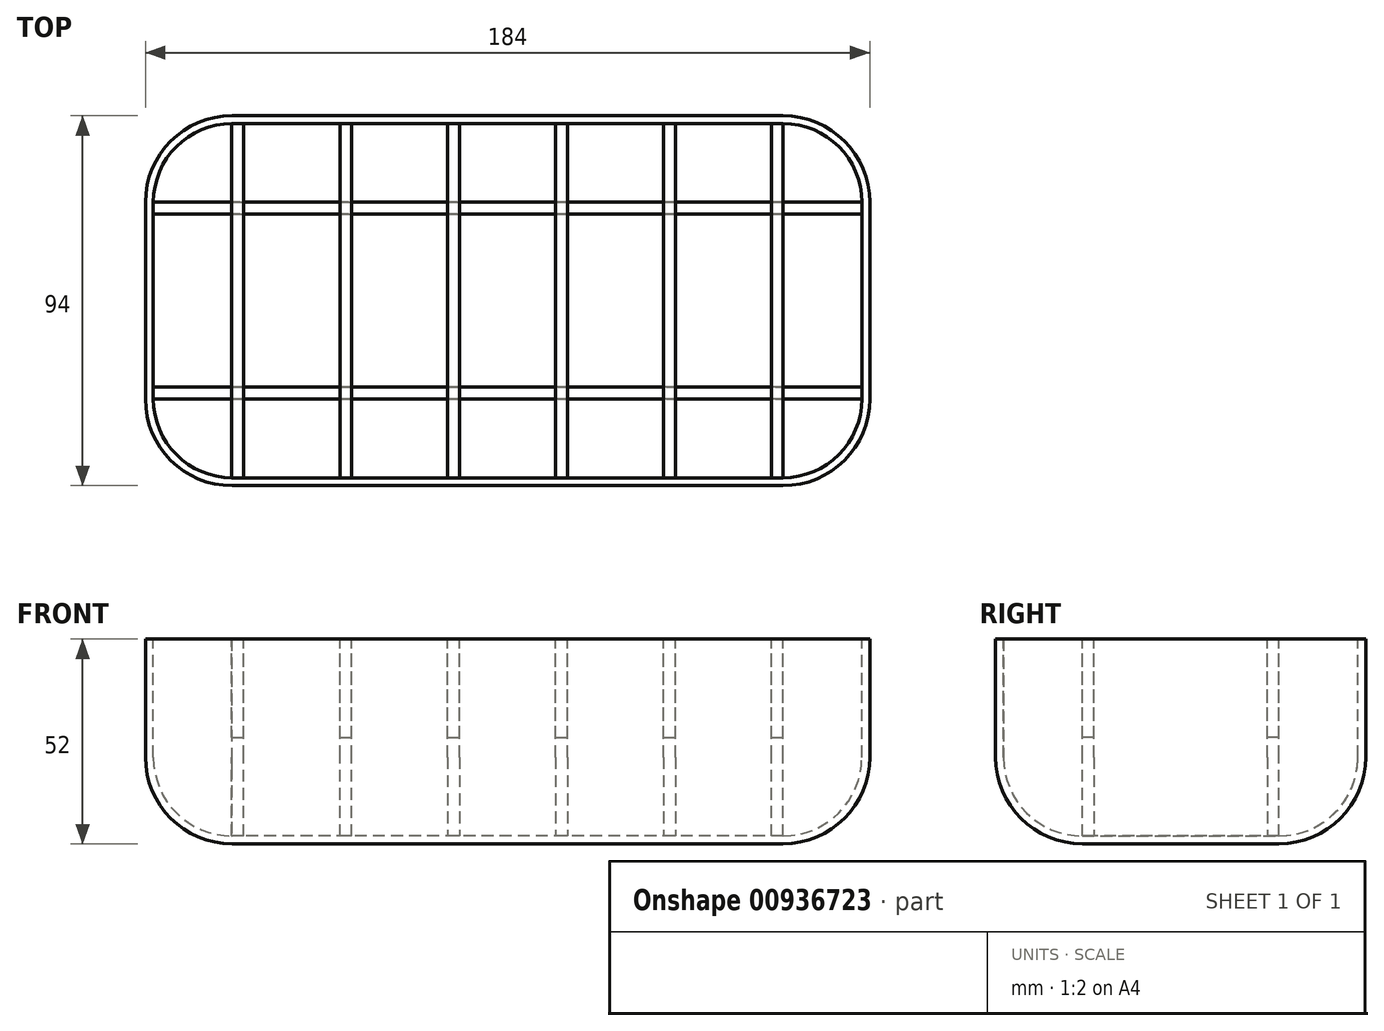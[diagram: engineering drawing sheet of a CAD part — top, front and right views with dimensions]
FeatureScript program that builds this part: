
annotation { "Feature Type Name" : "Feature", "Feature Type Description" : "" }
export const myFeature = defineFeature(function(context is Context, id is Id, definition is map)
    precondition{}
    {
        {
            var Q0;
            Q0=qCreatedBy(makeId("Top.planeOp"),FACE);
            var sketch = newSketch(context, id + "F0", { "sketchPlane" : qUnion([Q0])});
            skLineSegment(sketch, "E0.bottom", {"start": v(90, 45) * mm, "end": v(-90, 45) * mm});
            skLineSegment(sketch, "E0.top", {"start": v(90, -45) * mm, "end": v(-90, -45) * mm});
            skLineSegment(sketch, "E0.left", {"start": v(90, 45) * mm, "end": v(90, -45) * mm});
            skLineSegment(sketch, "E0.right", {"start": v(-90, 45) * mm, "end": v(-90, -45) * mm});
            skPoint(sketch, "E0.middle", {"position": v(0, 0) * mm});
            skSolve(sketch);
        }
        {
            var Q0;
            Q0=makeQuery(id+"F0.imprint","IMPRINT",FACE,{"disambiguationData":[TD([[makeQuery(id+"F0.imprint","IMPRINT",EDGE,{"derivedFrom":sQuery(id+"F0.wireOp",EDGE,"E0.bottom")}),1.0]])]});
            extrude(context, id + "F1", {"entities" : qUnion([Q0]), "oppositeDirection" : true, "depth" : 50 * mm, "offsetDistance" : 25 * mm});
        }
        {
            var Q0;
            Q0=makeQuery(id+"F1.opExtrude","CAP_EDGE",EDGE,{"disambiguationData":[OSD([sQuery(id+"F0.wireOp",EDGE,"E0.top")])],"isStart":false});
            var Q1;
            Q1=makeQuery(id+"F1.opExtrude","CAP_EDGE",EDGE,{"disambiguationData":[OSD([sQuery(id+"F0.wireOp",EDGE,"E0.left")])],"isStart":false});
            var Q2;
            Q2=makeQuery(id+"F1.opExtrude","CAP_EDGE",EDGE,{"disambiguationData":[OSD([sQuery(id+"F0.wireOp",EDGE,"E0.right")])],"isStart":false});
            var Q3;
            Q3=makeQuery(id+"F1.opExtrude","CAP_EDGE",EDGE,{"disambiguationData":[OSD([sQuery(id+"F0.wireOp",EDGE,"E0.bottom")])],"isStart":false});
            var Q4;
            Q4=makeQuery(id+"F1.opExtrude","SWEPT_EDGE",EDGE,{"disambiguationData":[OSD([sQuery(id+"F0.wireOp",EDGE,"E0.bottom"),sQuery(id+"F0.wireOp",EDGE,"E0.right")])]});
            var Q5;
            Q5=makeQuery(id+"F1.opExtrude","SWEPT_EDGE",EDGE,{"disambiguationData":[OSD([sQuery(id+"F0.wireOp",EDGE,"E0.bottom"),sQuery(id+"F0.wireOp",EDGE,"E0.left")])]});
            var Q6;
            Q6=makeQuery(id+"F1.opExtrude","SWEPT_EDGE",EDGE,{"disambiguationData":[OSD([sQuery(id+"F0.wireOp",EDGE,"E0.top"),sQuery(id+"F0.wireOp",EDGE,"E0.right")])]});
            var Q7;
            Q7=makeQuery(id+"F1.opExtrude","SWEPT_EDGE",EDGE,{"disambiguationData":[OSD([sQuery(id+"F0.wireOp",EDGE,"E0.top"),sQuery(id+"F0.wireOp",EDGE,"E0.left")])]});
            fillet(context, id + "F2", {"entities" : qUnion([Q0, Q1, Q2, Q3, Q4, Q5, Q6, Q7]), "radius" : 20 * mm, "tangentPropagation" : true, "allowEdgeOverflow" : false});
        }
        {
            var Q0;
            Q0=makeQuery(id+"F1.opExtrude","CAP_FACE",FACE,{"disambiguationData":[OSD([sQuery(id+"F0.wireOp",EDGE,"E0.bottom"),sQuery(id+"F0.wireOp",EDGE,"E0.top"),sQuery(id+"F0.wireOp",EDGE,"E0.left"),sQuery(id+"F0.wireOp",EDGE,"E0.right")])],"isStart":true});
            shell(context, id + "F3", {"entities" : qUnion([Q0]), "thickness" : 2 * mm, "oppositeDirection" : true});
        }
        {
            var Q0;
            Q0=makeQuery(id+"F1.opExtrude","CAP_FACE",FACE,{"disambiguationData":[OSD([sQuery(id+"F0.wireOp",EDGE,"E0.bottom"),sQuery(id+"F0.wireOp",EDGE,"E0.top"),sQuery(id+"F0.wireOp",EDGE,"E0.left"),sQuery(id+"F0.wireOp",EDGE,"E0.right")])],"isStart":true});
            var sketch = newSketch(context, id + "F4", { "sketchPlane" : qUnion([Q0])});
            skLineSegment(sketch, "E1", {"start": v(-90, 25) * mm, "end": v(90, 25) * mm});
            skLineSegment(sketch, "E2", {"start": v(90, -25) * mm, "end": v(-90, -25) * mm});
            skLineSegment(sketch, "E3", {"start": v(70, 45) * mm, "end": v(70, -45) * mm});
            skLineSegment(sketch, "E4.0", {"start": v(-67.06, 45) * mm, "end": v(-67.06, -45) * mm});
            skLineSegment(sketch, "E5.0", {"start": v(67, 45) * mm, "end": v(67, -45) * mm});
            skLineSegment(sketch, "E6.0", {"start": v(-90, 22) * mm, "end": v(90, 22) * mm});
            skLineSegment(sketch, "E7.0", {"start": v(90, -22) * mm, "end": v(-90, -22) * mm});
            skLineSegment(sketch, "E8.0", {"start": v(42.6, 45) * mm, "end": v(42.6, -45) * mm});
            skLineSegment(sketch, "E9.0", {"start": v(39.6, 45) * mm, "end": v(39.6, -45) * mm});
            skLineSegment(sketch, "E10.0", {"start": v(15.2, 45) * mm, "end": v(15.2, -45) * mm});
            skLineSegment(sketch, "E11.0", {"start": v(12.2, 45) * mm, "end": v(12.2, -45) * mm});
            skLineSegment(sketch, "E12.0", {"start": v(-12.2, 45) * mm, "end": v(-12.2, -45) * mm});
            skLineSegment(sketch, "E13.0", {"start": v(-15.2, 45) * mm, "end": v(-15.2, -45) * mm});
            skLineSegment(sketch, "E14.0", {"start": v(-39.6, 45) * mm, "end": v(-39.6, -45) * mm});
            skLineSegment(sketch, "E15.0", {"start": v(-42.6, 45) * mm, "end": v(-42.6, -45) * mm});
            skLineSegment(sketch, "E16.0", {"start": v(-70.06, 45) * mm, "end": v(-70.06, -45) * mm});
            skSolve(sketch);
        }
        {
            var Q0;
            {var subQ0=sQuery(id+"F4.wireOp",EDGE,"E1");var subQ7=sQuery(id+"F4.wireOp",EDGE,"E3");var subQ8=makeQuery(id+"F4.imprint","INTERSECT",VERTEX,{"derivedFrom":[subQ0,subQ7]});Q0=makeQuery(id+"F4.imprint","IMPRINT",FACE,{"disambiguationData":[TD([[makeQuery(id+"F4.imprint","IMPRINT",EDGE,{"disambiguationData":[TD([[subQ8,-1.0]])],"derivedFrom":subQ7}),1.0]])]});}
            var Q1;
            {var subQ0=sQuery(id+"F4.wireOp",EDGE,"E8.0");var subQ1=sQuery(id+"F4.wireOp",EDGE,"E1");var subQ2=makeQuery(id+"F4.imprint","INTERSECT",VERTEX,{"derivedFrom":[subQ1,subQ0]});Q1=makeQuery(id+"F4.imprint","IMPRINT",FACE,{"disambiguationData":[TD([[makeQuery(id+"F4.imprint","IMPRINT",EDGE,{"disambiguationData":[TD([[subQ2,-1.0]])],"derivedFrom":subQ1}),-1.0]])]});}
            var Q2;
            {var subQ0=sQuery(id+"F4.wireOp",EDGE,"E5.0");var subQ1=sQuery(id+"F4.wireOp",EDGE,"E1");var subQ2=makeQuery(id+"F4.imprint","INTERSECT",VERTEX,{"derivedFrom":[subQ1,subQ0]});Q2=makeQuery(id+"F4.imprint","IMPRINT",FACE,{"disambiguationData":[TD([[makeQuery(id+"F4.imprint","IMPRINT",EDGE,{"disambiguationData":[TD([[subQ2,-1.0]])],"derivedFrom":subQ1}),-1.0]])]});}
            var Q3;
            {var subQ0=sQuery(id+"F4.wireOp",EDGE,"E9.0");var subQ1=sQuery(id+"F4.wireOp",EDGE,"E1");var subQ2=makeQuery(id+"F4.imprint","INTERSECT",VERTEX,{"derivedFrom":[subQ1,subQ0]});Q3=makeQuery(id+"F4.imprint","IMPRINT",FACE,{"disambiguationData":[TD([[makeQuery(id+"F4.imprint","IMPRINT",EDGE,{"disambiguationData":[TD([[subQ2,-1.0]])],"derivedFrom":subQ1}),-1.0]])]});}
            var Q4;
            {var subQ0=sQuery(id+"F4.wireOp",EDGE,"E11.0");var subQ1=sQuery(id+"F4.wireOp",EDGE,"E1");var subQ2=makeQuery(id+"F4.imprint","INTERSECT",VERTEX,{"derivedFrom":[subQ1,subQ0]});Q4=makeQuery(id+"F4.imprint","IMPRINT",FACE,{"disambiguationData":[TD([[makeQuery(id+"F4.imprint","IMPRINT",EDGE,{"disambiguationData":[TD([[subQ2,-1.0]])],"derivedFrom":subQ1}),-1.0]])]});}
            var Q5;
            {var subQ0=sQuery(id+"F4.wireOp",EDGE,"E10.0");var subQ1=sQuery(id+"F4.wireOp",EDGE,"E1");var subQ2=makeQuery(id+"F4.imprint","INTERSECT",VERTEX,{"derivedFrom":[subQ1,subQ0]});Q5=makeQuery(id+"F4.imprint","IMPRINT",FACE,{"disambiguationData":[TD([[makeQuery(id+"F4.imprint","IMPRINT",EDGE,{"disambiguationData":[TD([[subQ2,-1.0]])],"derivedFrom":subQ1}),-1.0]])]});}
            var Q6;
            {var subQ0=sQuery(id+"F4.wireOp",EDGE,"E12.0");var subQ1=sQuery(id+"F4.wireOp",EDGE,"E1");var subQ2=makeQuery(id+"F4.imprint","INTERSECT",VERTEX,{"derivedFrom":[subQ1,subQ0]});Q6=makeQuery(id+"F4.imprint","IMPRINT",FACE,{"disambiguationData":[TD([[makeQuery(id+"F4.imprint","IMPRINT",EDGE,{"disambiguationData":[TD([[subQ2,-1.0]])],"derivedFrom":subQ1}),-1.0]])]});}
            var Q7;
            {var subQ0=sQuery(id+"F4.wireOp",EDGE,"E14.0");var subQ1=sQuery(id+"F4.wireOp",EDGE,"E1");var subQ2=makeQuery(id+"F4.imprint","INTERSECT",VERTEX,{"derivedFrom":[subQ1,subQ0]});Q7=makeQuery(id+"F4.imprint","IMPRINT",FACE,{"disambiguationData":[TD([[makeQuery(id+"F4.imprint","IMPRINT",EDGE,{"disambiguationData":[TD([[subQ2,-1.0]])],"derivedFrom":subQ1}),-1.0]])]});}
            var Q8;
            {var subQ0=sQuery(id+"F4.wireOp",EDGE,"E13.0");var subQ1=sQuery(id+"F4.wireOp",EDGE,"E1");var subQ2=makeQuery(id+"F4.imprint","INTERSECT",VERTEX,{"derivedFrom":[subQ1,subQ0]});Q8=makeQuery(id+"F4.imprint","IMPRINT",FACE,{"disambiguationData":[TD([[makeQuery(id+"F4.imprint","IMPRINT",EDGE,{"disambiguationData":[TD([[subQ2,-1.0]])],"derivedFrom":subQ1}),-1.0]])]});}
            var Q9;
            {var subQ0=sQuery(id+"F4.wireOp",EDGE,"E15.0");var subQ1=sQuery(id+"F4.wireOp",EDGE,"E1");var subQ2=makeQuery(id+"F4.imprint","INTERSECT",VERTEX,{"derivedFrom":[subQ1,subQ0]});Q9=makeQuery(id+"F4.imprint","IMPRINT",FACE,{"disambiguationData":[TD([[makeQuery(id+"F4.imprint","IMPRINT",EDGE,{"disambiguationData":[TD([[subQ2,-1.0]])],"derivedFrom":subQ1}),-1.0]])]});}
            var Q10;
            {var subQ0=sQuery(id+"F4.wireOp",EDGE,"E4.0");var subQ1=sQuery(id+"F4.wireOp",EDGE,"E1");var subQ2=makeQuery(id+"F4.imprint","INTERSECT",VERTEX,{"derivedFrom":[subQ1,subQ0]});Q10=makeQuery(id+"F4.imprint","IMPRINT",FACE,{"disambiguationData":[TD([[makeQuery(id+"F4.imprint","IMPRINT",EDGE,{"disambiguationData":[TD([[subQ2,-1.0]])],"derivedFrom":subQ1}),-1.0]])]});}
            var Q11;
            {var subQ0=sQuery(id+"F4.wireOp",EDGE,"E16.0");var subQ1=sQuery(id+"F4.wireOp",EDGE,"E1");var subQ2=makeQuery(id+"F4.imprint","INTERSECT",VERTEX,{"derivedFrom":[subQ1,subQ0]});Q11=makeQuery(id+"F4.imprint","IMPRINT",FACE,{"disambiguationData":[TD([[makeQuery(id+"F4.imprint","IMPRINT",EDGE,{"disambiguationData":[TD([[subQ2,-1.0]])],"derivedFrom":subQ1}),-1.0]])]});}
            var Q12;
            {var subQ0=sQuery(id+"F4.wireOp",EDGE,"E1");var subQ7=sQuery(id+"F4.wireOp",EDGE,"E16.0");var subQ8=makeQuery(id+"F4.imprint","INTERSECT",VERTEX,{"derivedFrom":[subQ0,subQ7]});Q12=makeQuery(id+"F4.imprint","IMPRINT",FACE,{"disambiguationData":[TD([[makeQuery(id+"F4.imprint","IMPRINT",EDGE,{"disambiguationData":[TD([[subQ8,-1.0]])],"derivedFrom":subQ7}),-1.0]])]});}
            var Q13;
            {var subQ0=sQuery(id+"F4.wireOp",EDGE,"ca702ad6-eab8-4127-9f72-cad6681242d5.0");var subQ1=sQuery(id+"F4.wireOp",EDGE,"E2");var subQ2=makeQuery(id+"F4.imprint","INTERSECT",VERTEX,{"derivedFrom":[subQ1,subQ0]});Q13=makeQuery(id+"F4.imprint","IMPRINT",FACE,{"disambiguationData":[TD([[makeQuery(id+"F4.imprint","IMPRINT",EDGE,{"disambiguationData":[TD([[subQ2,-1.0]])],"derivedFrom":subQ1}),-1.0]])]});}
            var Q14;
            {var subQ0=sQuery(id+"F4.wireOp",EDGE,"E15.0");var subQ1=sQuery(id+"F4.wireOp",EDGE,"E2");var subQ2=makeQuery(id+"F4.imprint","INTERSECT",VERTEX,{"derivedFrom":[subQ1,subQ0]});Q14=makeQuery(id+"F4.imprint","IMPRINT",FACE,{"disambiguationData":[TD([[makeQuery(id+"F4.imprint","IMPRINT",EDGE,{"disambiguationData":[TD([[subQ2,-1.0]])],"derivedFrom":subQ1}),-1.0]])]});}
            var Q15;
            {var subQ0=sQuery(id+"F4.wireOp",EDGE,"E14.0");var subQ1=sQuery(id+"F4.wireOp",EDGE,"E2");var subQ2=makeQuery(id+"F4.imprint","INTERSECT",VERTEX,{"derivedFrom":[subQ1,subQ0]});Q15=makeQuery(id+"F4.imprint","IMPRINT",FACE,{"disambiguationData":[TD([[makeQuery(id+"F4.imprint","IMPRINT",EDGE,{"disambiguationData":[TD([[subQ2,-1.0]])],"derivedFrom":subQ1}),-1.0]])]});}
            var Q16;
            {var subQ0=sQuery(id+"F4.wireOp",EDGE,"E2");var subQ7=sQuery(id+"F4.wireOp",EDGE,"E16.0");var subQ8=makeQuery(id+"F4.imprint","INTERSECT",VERTEX,{"derivedFrom":[subQ0,subQ7]});Q16=makeQuery(id+"F4.imprint","IMPRINT",FACE,{"disambiguationData":[TD([[makeQuery(id+"F4.imprint","IMPRINT",EDGE,{"disambiguationData":[TD([[subQ8,1.0]])],"derivedFrom":subQ7}),-1.0]])]});}
            var Q17;
            {var subQ0=sQuery(id+"F4.wireOp",EDGE,"E13.0");var subQ1=sQuery(id+"F4.wireOp",EDGE,"E2");var subQ2=makeQuery(id+"F4.imprint","INTERSECT",VERTEX,{"derivedFrom":[subQ1,subQ0]});Q17=makeQuery(id+"F4.imprint","IMPRINT",FACE,{"disambiguationData":[TD([[makeQuery(id+"F4.imprint","IMPRINT",EDGE,{"disambiguationData":[TD([[subQ2,-1.0]])],"derivedFrom":subQ1}),-1.0]])]});}
            var Q18;
            {var subQ0=sQuery(id+"F4.wireOp",EDGE,"E12.0");var subQ1=sQuery(id+"F4.wireOp",EDGE,"E2");var subQ2=makeQuery(id+"F4.imprint","INTERSECT",VERTEX,{"derivedFrom":[subQ1,subQ0]});Q18=makeQuery(id+"F4.imprint","IMPRINT",FACE,{"disambiguationData":[TD([[makeQuery(id+"F4.imprint","IMPRINT",EDGE,{"disambiguationData":[TD([[subQ2,-1.0]])],"derivedFrom":subQ1}),-1.0]])]});}
            var Q19;
            {var subQ0=sQuery(id+"F4.wireOp",EDGE,"E11.0");var subQ1=sQuery(id+"F4.wireOp",EDGE,"E2");var subQ2=makeQuery(id+"F4.imprint","INTERSECT",VERTEX,{"derivedFrom":[subQ1,subQ0]});Q19=makeQuery(id+"F4.imprint","IMPRINT",FACE,{"disambiguationData":[TD([[makeQuery(id+"F4.imprint","IMPRINT",EDGE,{"disambiguationData":[TD([[subQ2,-1.0]])],"derivedFrom":subQ1}),-1.0]])]});}
            var Q20;
            {var subQ0=sQuery(id+"F4.wireOp",EDGE,"E9.0");var subQ1=sQuery(id+"F4.wireOp",EDGE,"E2");var subQ2=makeQuery(id+"F4.imprint","INTERSECT",VERTEX,{"derivedFrom":[subQ1,subQ0]});Q20=makeQuery(id+"F4.imprint","IMPRINT",FACE,{"disambiguationData":[TD([[makeQuery(id+"F4.imprint","IMPRINT",EDGE,{"disambiguationData":[TD([[subQ2,-1.0]])],"derivedFrom":subQ1}),-1.0]])]});}
            var Q21;
            {var subQ0=sQuery(id+"F4.wireOp",EDGE,"E10.0");var subQ1=sQuery(id+"F4.wireOp",EDGE,"E2");var subQ2=makeQuery(id+"F4.imprint","INTERSECT",VERTEX,{"derivedFrom":[subQ1,subQ0]});Q21=makeQuery(id+"F4.imprint","IMPRINT",FACE,{"disambiguationData":[TD([[makeQuery(id+"F4.imprint","IMPRINT",EDGE,{"disambiguationData":[TD([[subQ2,-1.0]])],"derivedFrom":subQ1}),-1.0]])]});}
            var Q22;
            {var subQ0=sQuery(id+"F4.wireOp",EDGE,"E8.0");var subQ1=sQuery(id+"F4.wireOp",EDGE,"E2");var subQ2=makeQuery(id+"F4.imprint","INTERSECT",VERTEX,{"derivedFrom":[subQ1,subQ0]});Q22=makeQuery(id+"F4.imprint","IMPRINT",FACE,{"disambiguationData":[TD([[makeQuery(id+"F4.imprint","IMPRINT",EDGE,{"disambiguationData":[TD([[subQ2,-1.0]])],"derivedFrom":subQ1}),-1.0]])]});}
            var Q23;
            {var subQ0=sQuery(id+"F4.wireOp",EDGE,"E5.0");var subQ1=sQuery(id+"F4.wireOp",EDGE,"E2");var subQ2=makeQuery(id+"F4.imprint","INTERSECT",VERTEX,{"derivedFrom":[subQ1,subQ0]});Q23=makeQuery(id+"F4.imprint","IMPRINT",FACE,{"disambiguationData":[TD([[makeQuery(id+"F4.imprint","IMPRINT",EDGE,{"disambiguationData":[TD([[subQ2,-1.0]])],"derivedFrom":subQ1}),-1.0]])]});}
            var Q24;
            {var subQ0=sQuery(id+"F4.wireOp",EDGE,"E3");var subQ1=sQuery(id+"F4.wireOp",EDGE,"E2");var subQ2=makeQuery(id+"F4.imprint","INTERSECT",VERTEX,{"derivedFrom":[subQ1,subQ0]});Q24=makeQuery(id+"F4.imprint","IMPRINT",FACE,{"disambiguationData":[TD([[makeQuery(id+"F4.imprint","IMPRINT",EDGE,{"disambiguationData":[TD([[subQ2,-1.0]])],"derivedFrom":subQ1}),-1.0]])]});}
            var Q25;
            {var subQ0=sQuery(id+"F4.wireOp",EDGE,"E2");var subQ7=sQuery(id+"F4.wireOp",EDGE,"E3");var subQ8=makeQuery(id+"F4.imprint","INTERSECT",VERTEX,{"derivedFrom":[subQ0,subQ7]});Q25=makeQuery(id+"F4.imprint","IMPRINT",FACE,{"disambiguationData":[TD([[makeQuery(id+"F4.imprint","IMPRINT",EDGE,{"disambiguationData":[TD([[subQ8,1.0]])],"derivedFrom":subQ7}),1.0]])]});}
            extrude(context, id + "F5", {"entities" : qUnion([Q0, Q1, Q2, Q3, Q4, Q5, Q6, Q7, Q8, Q9, Q10, Q11, Q12, Q13, Q14, Q15, Q16, Q17, Q18, Q19, Q20, Q21, Q22, Q23, Q24, Q25]), "endBound" : BoundingType.UP_TO_NEXT, "oppositeDirection" : true, "depth" : 25 * mm, "offsetDistance" : 25 * mm});
        }
        {
            var Q0;
            {var subQ0=sQuery(id+"F4.wireOp",EDGE,"E16.0");var subQ1=sQuery(id+"F4.wireOp",EDGE,"E1");var subQ2=makeQuery(id+"F4.imprint","INTERSECT",VERTEX,{"derivedFrom":[subQ1,subQ0]});Q0=makeQuery(id+"F4.imprint","IMPRINT",FACE,{"disambiguationData":[TD([[makeQuery(id+"F4.imprint","IMPRINT",EDGE,{"disambiguationData":[TD([[subQ2,-1.0]])],"derivedFrom":subQ1}),-1.0]])]});}
            var Q1;
            {var subQ0=sQuery(id+"F4.wireOp",EDGE,"E15.0");var subQ1=sQuery(id+"F4.wireOp",EDGE,"E1");var subQ2=makeQuery(id+"F4.imprint","INTERSECT",VERTEX,{"derivedFrom":[subQ1,subQ0]});Q1=makeQuery(id+"F4.imprint","IMPRINT",FACE,{"disambiguationData":[TD([[makeQuery(id+"F4.imprint","IMPRINT",EDGE,{"disambiguationData":[TD([[subQ2,-1.0]])],"derivedFrom":subQ1}),-1.0]])]});}
            var Q2;
            {var subQ0=sQuery(id+"F4.wireOp",EDGE,"E4.0");var subQ1=sQuery(id+"F4.wireOp",EDGE,"E2");var subQ2=makeQuery(id+"F4.imprint","INTERSECT",VERTEX,{"derivedFrom":[subQ1,subQ0]});Q2=makeQuery(id+"F4.imprint","IMPRINT",FACE,{"disambiguationData":[TD([[makeQuery(id+"F4.imprint","IMPRINT",EDGE,{"disambiguationData":[TD([[subQ2,-1.0]])],"derivedFrom":subQ1}),-1.0]])]});}
            var Q3;
            {var subQ0=sQuery(id+"F4.wireOp",EDGE,"E14.0");var subQ1=sQuery(id+"F4.wireOp",EDGE,"E2");var subQ2=makeQuery(id+"F4.imprint","INTERSECT",VERTEX,{"derivedFrom":[subQ1,subQ0]});Q3=makeQuery(id+"F4.imprint","IMPRINT",FACE,{"disambiguationData":[TD([[makeQuery(id+"F4.imprint","IMPRINT",EDGE,{"disambiguationData":[TD([[subQ2,-1.0]])],"derivedFrom":subQ1}),-1.0]])]});}
            var Q4;
            {var subQ0=sQuery(id+"F4.wireOp",EDGE,"E12.0");var subQ1=sQuery(id+"F4.wireOp",EDGE,"E2");var subQ2=makeQuery(id+"F4.imprint","INTERSECT",VERTEX,{"derivedFrom":[subQ1,subQ0]});Q4=makeQuery(id+"F4.imprint","IMPRINT",FACE,{"disambiguationData":[TD([[makeQuery(id+"F4.imprint","IMPRINT",EDGE,{"disambiguationData":[TD([[subQ2,-1.0]])],"derivedFrom":subQ1}),-1.0]])]});}
            var Q5;
            {var subQ0=sQuery(id+"F4.wireOp",EDGE,"E10.0");var subQ1=sQuery(id+"F4.wireOp",EDGE,"E2");var subQ2=makeQuery(id+"F4.imprint","INTERSECT",VERTEX,{"derivedFrom":[subQ1,subQ0]});Q5=makeQuery(id+"F4.imprint","IMPRINT",FACE,{"disambiguationData":[TD([[makeQuery(id+"F4.imprint","IMPRINT",EDGE,{"disambiguationData":[TD([[subQ2,-1.0]])],"derivedFrom":subQ1}),-1.0]])]});}
            var Q6;
            {var subQ0=sQuery(id+"F4.wireOp",EDGE,"E13.0");var subQ1=sQuery(id+"F4.wireOp",EDGE,"E1");var subQ2=makeQuery(id+"F4.imprint","INTERSECT",VERTEX,{"derivedFrom":[subQ1,subQ0]});Q6=makeQuery(id+"F4.imprint","IMPRINT",FACE,{"disambiguationData":[TD([[makeQuery(id+"F4.imprint","IMPRINT",EDGE,{"disambiguationData":[TD([[subQ2,-1.0]])],"derivedFrom":subQ1}),-1.0]])]});}
            var Q7;
            {var subQ0=sQuery(id+"F4.wireOp",EDGE,"E11.0");var subQ1=sQuery(id+"F4.wireOp",EDGE,"E1");var subQ2=makeQuery(id+"F4.imprint","INTERSECT",VERTEX,{"derivedFrom":[subQ1,subQ0]});Q7=makeQuery(id+"F4.imprint","IMPRINT",FACE,{"disambiguationData":[TD([[makeQuery(id+"F4.imprint","IMPRINT",EDGE,{"disambiguationData":[TD([[subQ2,-1.0]])],"derivedFrom":subQ1}),-1.0]])]});}
            var Q8;
            {var subQ0=sQuery(id+"F4.wireOp",EDGE,"E9.0");var subQ1=sQuery(id+"F4.wireOp",EDGE,"E1");var subQ2=makeQuery(id+"F4.imprint","INTERSECT",VERTEX,{"derivedFrom":[subQ1,subQ0]});Q8=makeQuery(id+"F4.imprint","IMPRINT",FACE,{"disambiguationData":[TD([[makeQuery(id+"F4.imprint","IMPRINT",EDGE,{"disambiguationData":[TD([[subQ2,-1.0]])],"derivedFrom":subQ1}),-1.0]])]});}
            var Q9;
            {var subQ0=sQuery(id+"F4.wireOp",EDGE,"E5.0");var subQ1=sQuery(id+"F4.wireOp",EDGE,"E1");var subQ2=makeQuery(id+"F4.imprint","INTERSECT",VERTEX,{"derivedFrom":[subQ1,subQ0]});Q9=makeQuery(id+"F4.imprint","IMPRINT",FACE,{"disambiguationData":[TD([[makeQuery(id+"F4.imprint","IMPRINT",EDGE,{"disambiguationData":[TD([[subQ2,-1.0]])],"derivedFrom":subQ1}),-1.0]])]});}
            var Q10;
            {var subQ0=sQuery(id+"F4.wireOp",EDGE,"E3");var subQ1=sQuery(id+"F4.wireOp",EDGE,"E2");var subQ2=makeQuery(id+"F4.imprint","INTERSECT",VERTEX,{"derivedFrom":[subQ1,subQ0]});Q10=makeQuery(id+"F4.imprint","IMPRINT",FACE,{"disambiguationData":[TD([[makeQuery(id+"F4.imprint","IMPRINT",EDGE,{"disambiguationData":[TD([[subQ2,-1.0]])],"derivedFrom":subQ1}),-1.0]])]});}
            var Q11;
            {var subQ0=sQuery(id+"F4.wireOp",EDGE,"E8.0");var subQ1=sQuery(id+"F4.wireOp",EDGE,"E2");var subQ2=makeQuery(id+"F4.imprint","INTERSECT",VERTEX,{"derivedFrom":[subQ1,subQ0]});Q11=makeQuery(id+"F4.imprint","IMPRINT",FACE,{"disambiguationData":[TD([[makeQuery(id+"F4.imprint","IMPRINT",EDGE,{"disambiguationData":[TD([[subQ2,-1.0]])],"derivedFrom":subQ1}),-1.0]])]});}
            extrude(context, id + "F6", {"entities" : qUnion([Q0, Q1, Q2, Q3, Q4, Q5, Q6, Q7, Q8, Q9, Q10, Q11]), "operationType" : NewBodyOperationType.REMOVE, "oppositeDirection" : true, "depth" : 25 * mm, "offsetDistance" : 25 * mm});
        }
        {
            var Q0;
            {var subQ0=sQuery(id+"F4.wireOp",EDGE,"E6.0");var subQ1=sQuery(id+"F4.wireOp",EDGE,"E3");var subQ2=makeQuery(id+"F4.imprint","INTERSECT",VERTEX,{"derivedFrom":[subQ1,subQ0]});Q0=makeQuery(id+"F4.imprint","IMPRINT",FACE,{"disambiguationData":[TD([[makeQuery(id+"F4.imprint","IMPRINT",EDGE,{"disambiguationData":[TD([[subQ2,-1.0]])],"derivedFrom":subQ1}),-1.0]])]});}
            var Q1;
            {var subQ0=sQuery(id+"F4.wireOp",EDGE,"E3");var subQ1=sQuery(id+"F4.wireOp",EDGE,"E2");var subQ2=makeQuery(id+"F4.imprint","INTERSECT",VERTEX,{"derivedFrom":[subQ1,subQ0]});Q1=makeQuery(id+"F4.imprint","IMPRINT",FACE,{"disambiguationData":[TD([[makeQuery(id+"F4.imprint","IMPRINT",EDGE,{"disambiguationData":[TD([[subQ2,-1.0]])],"derivedFrom":subQ1}),1.0]])]});}
            var Q2;
            {var subQ0=sQuery(id+"F4.wireOp",EDGE,"E3");var subQ1=sQuery(id+"F4.wireOp",EDGE,"E2");var subQ2=makeQuery(id+"F4.imprint","INTERSECT",VERTEX,{"derivedFrom":[subQ1,subQ0]});Q2=makeQuery(id+"F4.imprint","IMPRINT",FACE,{"disambiguationData":[TD([[makeQuery(id+"F4.imprint","IMPRINT",EDGE,{"disambiguationData":[TD([[subQ2,-1.0]])],"derivedFrom":subQ1}),-1.0]])]});}
            var Q3;
            {var subQ0=sQuery(id+"F4.wireOp",EDGE,"E5.0");var subQ1=sQuery(id+"F4.wireOp",EDGE,"E1");var subQ2=makeQuery(id+"F4.imprint","INTERSECT",VERTEX,{"derivedFrom":[subQ1,subQ0]});Q3=makeQuery(id+"F4.imprint","IMPRINT",FACE,{"disambiguationData":[TD([[makeQuery(id+"F4.imprint","IMPRINT",EDGE,{"disambiguationData":[TD([[subQ2,-1.0]])],"derivedFrom":subQ1}),-1.0]])]});}
            var Q4;
            {var subQ0=sQuery(id+"F4.wireOp",EDGE,"E5.0");var subQ1=sQuery(id+"F4.wireOp",EDGE,"E1");var subQ2=makeQuery(id+"F4.imprint","INTERSECT",VERTEX,{"derivedFrom":[subQ1,subQ0]});Q4=makeQuery(id+"F4.imprint","IMPRINT",FACE,{"disambiguationData":[TD([[makeQuery(id+"F4.imprint","IMPRINT",EDGE,{"disambiguationData":[TD([[subQ2,-1.0]])],"derivedFrom":subQ1}),1.0]])]});}
            var Q5;
            {var subQ0=sQuery(id+"F4.wireOp",EDGE,"E9.0");var subQ1=sQuery(id+"F4.wireOp",EDGE,"E1");var subQ2=makeQuery(id+"F4.imprint","INTERSECT",VERTEX,{"derivedFrom":[subQ1,subQ0]});Q5=makeQuery(id+"F4.imprint","IMPRINT",FACE,{"disambiguationData":[TD([[makeQuery(id+"F4.imprint","IMPRINT",EDGE,{"disambiguationData":[TD([[subQ2,-1.0]])],"derivedFrom":subQ1}),1.0]])]});}
            var Q6;
            {var subQ0=sQuery(id+"F4.wireOp",EDGE,"E9.0");var subQ1=sQuery(id+"F4.wireOp",EDGE,"E1");var subQ2=makeQuery(id+"F4.imprint","INTERSECT",VERTEX,{"derivedFrom":[subQ1,subQ0]});Q6=makeQuery(id+"F4.imprint","IMPRINT",FACE,{"disambiguationData":[TD([[makeQuery(id+"F4.imprint","IMPRINT",EDGE,{"disambiguationData":[TD([[subQ2,-1.0]])],"derivedFrom":subQ1}),-1.0]])]});}
            var Q7;
            {var subQ0=sQuery(id+"F4.wireOp",EDGE,"E9.0");var subQ1=sQuery(id+"F4.wireOp",EDGE,"E6.0");var subQ2=makeQuery(id+"F4.imprint","INTERSECT",VERTEX,{"derivedFrom":[subQ1,subQ0]});Q7=makeQuery(id+"F4.imprint","IMPRINT",FACE,{"disambiguationData":[TD([[makeQuery(id+"F4.imprint","IMPRINT",EDGE,{"disambiguationData":[TD([[subQ2,-1.0]])],"derivedFrom":subQ1}),-1.0]])]});}
            var Q8;
            {var subQ0=sQuery(id+"F4.wireOp",EDGE,"E8.0");var subQ1=sQuery(id+"F4.wireOp",EDGE,"E2");var subQ2=makeQuery(id+"F4.imprint","INTERSECT",VERTEX,{"derivedFrom":[subQ1,subQ0]});Q8=makeQuery(id+"F4.imprint","IMPRINT",FACE,{"disambiguationData":[TD([[makeQuery(id+"F4.imprint","IMPRINT",EDGE,{"disambiguationData":[TD([[subQ2,-1.0]])],"derivedFrom":subQ1}),1.0]])]});}
            var Q9;
            {var subQ0=sQuery(id+"F4.wireOp",EDGE,"E8.0");var subQ1=sQuery(id+"F4.wireOp",EDGE,"E2");var subQ2=makeQuery(id+"F4.imprint","INTERSECT",VERTEX,{"derivedFrom":[subQ1,subQ0]});Q9=makeQuery(id+"F4.imprint","IMPRINT",FACE,{"disambiguationData":[TD([[makeQuery(id+"F4.imprint","IMPRINT",EDGE,{"disambiguationData":[TD([[subQ2,-1.0]])],"derivedFrom":subQ1}),-1.0]])]});}
            var Q10;
            {var subQ0=sQuery(id+"F4.wireOp",EDGE,"E10.0");var subQ1=sQuery(id+"F4.wireOp",EDGE,"E2");var subQ2=makeQuery(id+"F4.imprint","INTERSECT",VERTEX,{"derivedFrom":[subQ1,subQ0]});Q10=makeQuery(id+"F4.imprint","IMPRINT",FACE,{"disambiguationData":[TD([[makeQuery(id+"F4.imprint","IMPRINT",EDGE,{"disambiguationData":[TD([[subQ2,-1.0]])],"derivedFrom":subQ1}),-1.0]])]});}
            var Q11;
            {var subQ0=sQuery(id+"F4.wireOp",EDGE,"E10.0");var subQ1=sQuery(id+"F4.wireOp",EDGE,"E2");var subQ2=makeQuery(id+"F4.imprint","INTERSECT",VERTEX,{"derivedFrom":[subQ1,subQ0]});Q11=makeQuery(id+"F4.imprint","IMPRINT",FACE,{"disambiguationData":[TD([[makeQuery(id+"F4.imprint","IMPRINT",EDGE,{"disambiguationData":[TD([[subQ2,-1.0]])],"derivedFrom":subQ1}),1.0]])]});}
            var Q12;
            {var subQ0=sQuery(id+"F4.wireOp",EDGE,"E11.0");var subQ1=sQuery(id+"F4.wireOp",EDGE,"E6.0");var subQ2=makeQuery(id+"F4.imprint","INTERSECT",VERTEX,{"derivedFrom":[subQ1,subQ0]});Q12=makeQuery(id+"F4.imprint","IMPRINT",FACE,{"disambiguationData":[TD([[makeQuery(id+"F4.imprint","IMPRINT",EDGE,{"disambiguationData":[TD([[subQ2,-1.0]])],"derivedFrom":subQ1}),-1.0]])]});}
            var Q13;
            {var subQ0=sQuery(id+"F4.wireOp",EDGE,"E11.0");var subQ1=sQuery(id+"F4.wireOp",EDGE,"E1");var subQ2=makeQuery(id+"F4.imprint","INTERSECT",VERTEX,{"derivedFrom":[subQ1,subQ0]});Q13=makeQuery(id+"F4.imprint","IMPRINT",FACE,{"disambiguationData":[TD([[makeQuery(id+"F4.imprint","IMPRINT",EDGE,{"disambiguationData":[TD([[subQ2,-1.0]])],"derivedFrom":subQ1}),1.0]])]});}
            var Q14;
            {var subQ0=sQuery(id+"F4.wireOp",EDGE,"E11.0");var subQ1=sQuery(id+"F4.wireOp",EDGE,"E1");var subQ2=makeQuery(id+"F4.imprint","INTERSECT",VERTEX,{"derivedFrom":[subQ1,subQ0]});Q14=makeQuery(id+"F4.imprint","IMPRINT",FACE,{"disambiguationData":[TD([[makeQuery(id+"F4.imprint","IMPRINT",EDGE,{"disambiguationData":[TD([[subQ2,-1.0]])],"derivedFrom":subQ1}),-1.0]])]});}
            var Q15;
            {var subQ0=sQuery(id+"F4.wireOp",EDGE,"E13.0");var subQ1=sQuery(id+"F4.wireOp",EDGE,"E1");var subQ2=makeQuery(id+"F4.imprint","INTERSECT",VERTEX,{"derivedFrom":[subQ1,subQ0]});Q15=makeQuery(id+"F4.imprint","IMPRINT",FACE,{"disambiguationData":[TD([[makeQuery(id+"F4.imprint","IMPRINT",EDGE,{"disambiguationData":[TD([[subQ2,-1.0]])],"derivedFrom":subQ1}),1.0]])]});}
            var Q16;
            {var subQ0=sQuery(id+"F4.wireOp",EDGE,"E13.0");var subQ1=sQuery(id+"F4.wireOp",EDGE,"E1");var subQ2=makeQuery(id+"F4.imprint","INTERSECT",VERTEX,{"derivedFrom":[subQ1,subQ0]});Q16=makeQuery(id+"F4.imprint","IMPRINT",FACE,{"disambiguationData":[TD([[makeQuery(id+"F4.imprint","IMPRINT",EDGE,{"disambiguationData":[TD([[subQ2,-1.0]])],"derivedFrom":subQ1}),-1.0]])]});}
            var Q17;
            {var subQ0=sQuery(id+"F4.wireOp",EDGE,"E13.0");var subQ1=sQuery(id+"F4.wireOp",EDGE,"E6.0");var subQ2=makeQuery(id+"F4.imprint","INTERSECT",VERTEX,{"derivedFrom":[subQ1,subQ0]});Q17=makeQuery(id+"F4.imprint","IMPRINT",FACE,{"disambiguationData":[TD([[makeQuery(id+"F4.imprint","IMPRINT",EDGE,{"disambiguationData":[TD([[subQ2,-1.0]])],"derivedFrom":subQ1}),-1.0]])]});}
            var Q18;
            {var subQ0=sQuery(id+"F4.wireOp",EDGE,"E12.0");var subQ1=sQuery(id+"F4.wireOp",EDGE,"E2");var subQ2=makeQuery(id+"F4.imprint","INTERSECT",VERTEX,{"derivedFrom":[subQ1,subQ0]});Q18=makeQuery(id+"F4.imprint","IMPRINT",FACE,{"disambiguationData":[TD([[makeQuery(id+"F4.imprint","IMPRINT",EDGE,{"disambiguationData":[TD([[subQ2,-1.0]])],"derivedFrom":subQ1}),-1.0]])]});}
            var Q19;
            {var subQ0=sQuery(id+"F4.wireOp",EDGE,"E12.0");var subQ1=sQuery(id+"F4.wireOp",EDGE,"E2");var subQ2=makeQuery(id+"F4.imprint","INTERSECT",VERTEX,{"derivedFrom":[subQ1,subQ0]});Q19=makeQuery(id+"F4.imprint","IMPRINT",FACE,{"disambiguationData":[TD([[makeQuery(id+"F4.imprint","IMPRINT",EDGE,{"disambiguationData":[TD([[subQ2,-1.0]])],"derivedFrom":subQ1}),1.0]])]});}
            var Q20;
            {var subQ0=sQuery(id+"F4.wireOp",EDGE,"E14.0");var subQ1=sQuery(id+"F4.wireOp",EDGE,"E2");var subQ2=makeQuery(id+"F4.imprint","INTERSECT",VERTEX,{"derivedFrom":[subQ1,subQ0]});Q20=makeQuery(id+"F4.imprint","IMPRINT",FACE,{"disambiguationData":[TD([[makeQuery(id+"F4.imprint","IMPRINT",EDGE,{"disambiguationData":[TD([[subQ2,-1.0]])],"derivedFrom":subQ1}),1.0]])]});}
            var Q21;
            {var subQ0=sQuery(id+"F4.wireOp",EDGE,"E15.0");var subQ1=sQuery(id+"F4.wireOp",EDGE,"E6.0");var subQ2=makeQuery(id+"F4.imprint","INTERSECT",VERTEX,{"derivedFrom":[subQ1,subQ0]});Q21=makeQuery(id+"F4.imprint","IMPRINT",FACE,{"disambiguationData":[TD([[makeQuery(id+"F4.imprint","IMPRINT",EDGE,{"disambiguationData":[TD([[subQ2,-1.0]])],"derivedFrom":subQ1}),-1.0]])]});}
            var Q22;
            {var subQ0=sQuery(id+"F4.wireOp",EDGE,"E14.0");var subQ1=sQuery(id+"F4.wireOp",EDGE,"E2");var subQ2=makeQuery(id+"F4.imprint","INTERSECT",VERTEX,{"derivedFrom":[subQ1,subQ0]});Q22=makeQuery(id+"F4.imprint","IMPRINT",FACE,{"disambiguationData":[TD([[makeQuery(id+"F4.imprint","IMPRINT",EDGE,{"disambiguationData":[TD([[subQ2,-1.0]])],"derivedFrom":subQ1}),-1.0]])]});}
            var Q23;
            {var subQ0=sQuery(id+"F4.wireOp",EDGE,"E15.0");var subQ1=sQuery(id+"F4.wireOp",EDGE,"E1");var subQ2=makeQuery(id+"F4.imprint","INTERSECT",VERTEX,{"derivedFrom":[subQ1,subQ0]});Q23=makeQuery(id+"F4.imprint","IMPRINT",FACE,{"disambiguationData":[TD([[makeQuery(id+"F4.imprint","IMPRINT",EDGE,{"disambiguationData":[TD([[subQ2,-1.0]])],"derivedFrom":subQ1}),1.0]])]});}
            var Q24;
            {var subQ0=sQuery(id+"F4.wireOp",EDGE,"E15.0");var subQ1=sQuery(id+"F4.wireOp",EDGE,"E1");var subQ2=makeQuery(id+"F4.imprint","INTERSECT",VERTEX,{"derivedFrom":[subQ1,subQ0]});Q24=makeQuery(id+"F4.imprint","IMPRINT",FACE,{"disambiguationData":[TD([[makeQuery(id+"F4.imprint","IMPRINT",EDGE,{"disambiguationData":[TD([[subQ2,-1.0]])],"derivedFrom":subQ1}),-1.0]])]});}
            var Q25;
            {var subQ0=sQuery(id+"F4.wireOp",EDGE,"E16.0");var subQ1=sQuery(id+"F4.wireOp",EDGE,"E1");var subQ2=makeQuery(id+"F4.imprint","INTERSECT",VERTEX,{"derivedFrom":[subQ1,subQ0]});Q25=makeQuery(id+"F4.imprint","IMPRINT",FACE,{"disambiguationData":[TD([[makeQuery(id+"F4.imprint","IMPRINT",EDGE,{"disambiguationData":[TD([[subQ2,-1.0]])],"derivedFrom":subQ1}),-1.0]])]});}
            var Q26;
            {var subQ0=sQuery(id+"F4.wireOp",EDGE,"E6.0");var subQ1=sQuery(id+"F4.wireOp",EDGE,"E4.0");var subQ2=makeQuery(id+"F4.imprint","INTERSECT",VERTEX,{"derivedFrom":[subQ1,subQ0]});Q26=makeQuery(id+"F4.imprint","IMPRINT",FACE,{"disambiguationData":[TD([[makeQuery(id+"F4.imprint","IMPRINT",EDGE,{"disambiguationData":[TD([[subQ2,-1.0]])],"derivedFrom":subQ1}),-1.0]])]});}
            var Q27;
            {var subQ7=sQuery(id+"F4.wireOp",EDGE,"E16.0");var subQ9=sQuery(id+"F4.wireOp",EDGE,"E1");var subQ10=makeQuery(id+"F4.imprint","INTERSECT",VERTEX,{"derivedFrom":[subQ9,subQ7]});Q27=makeQuery(id+"F4.imprint","IMPRINT",FACE,{"disambiguationData":[TD([[makeQuery(id+"F4.imprint","IMPRINT",EDGE,{"disambiguationData":[TD([[subQ10,-1.0]])],"derivedFrom":subQ9}),1.0]])]});}
            var Q28;
            {var subQ0=sQuery(id+"F4.wireOp",EDGE,"E4.0");var subQ1=sQuery(id+"F4.wireOp",EDGE,"E2");var subQ2=makeQuery(id+"F4.imprint","INTERSECT",VERTEX,{"derivedFrom":[subQ1,subQ0]});Q28=makeQuery(id+"F4.imprint","IMPRINT",FACE,{"disambiguationData":[TD([[makeQuery(id+"F4.imprint","IMPRINT",EDGE,{"disambiguationData":[TD([[subQ2,-1.0]])],"derivedFrom":subQ1}),-1.0]])]});}
            var Q29;
            {var subQ7=sQuery(id+"F4.wireOp",EDGE,"E2");var subQ9=sQuery(id+"F4.wireOp",EDGE,"E4.0");var subQ12=makeQuery(id+"F4.imprint","INTERSECT",VERTEX,{"derivedFrom":[subQ7,subQ9]});Q29=makeQuery(id+"F4.imprint","IMPRINT",FACE,{"disambiguationData":[TD([[makeQuery(id+"F4.imprint","IMPRINT",EDGE,{"disambiguationData":[TD([[subQ12,-1.0]])],"derivedFrom":subQ7}),1.0]])]});}
            extrude(context, id + "F7", {"entities" : qUnion([Q0, Q1, Q2, Q3, Q4, Q5, Q6, Q7, Q8, Q9, Q10, Q11, Q12, Q13, Q14, Q15, Q16, Q17, Q18, Q19, Q20, Q21, Q22, Q23, Q24, Q25, Q26, Q27, Q28, Q29]), "endBound" : BoundingType.UP_TO_NEXT, "oppositeDirection" : true, "depth" : 25 * mm, "offsetDistance" : 25 * mm});
        }
    });
